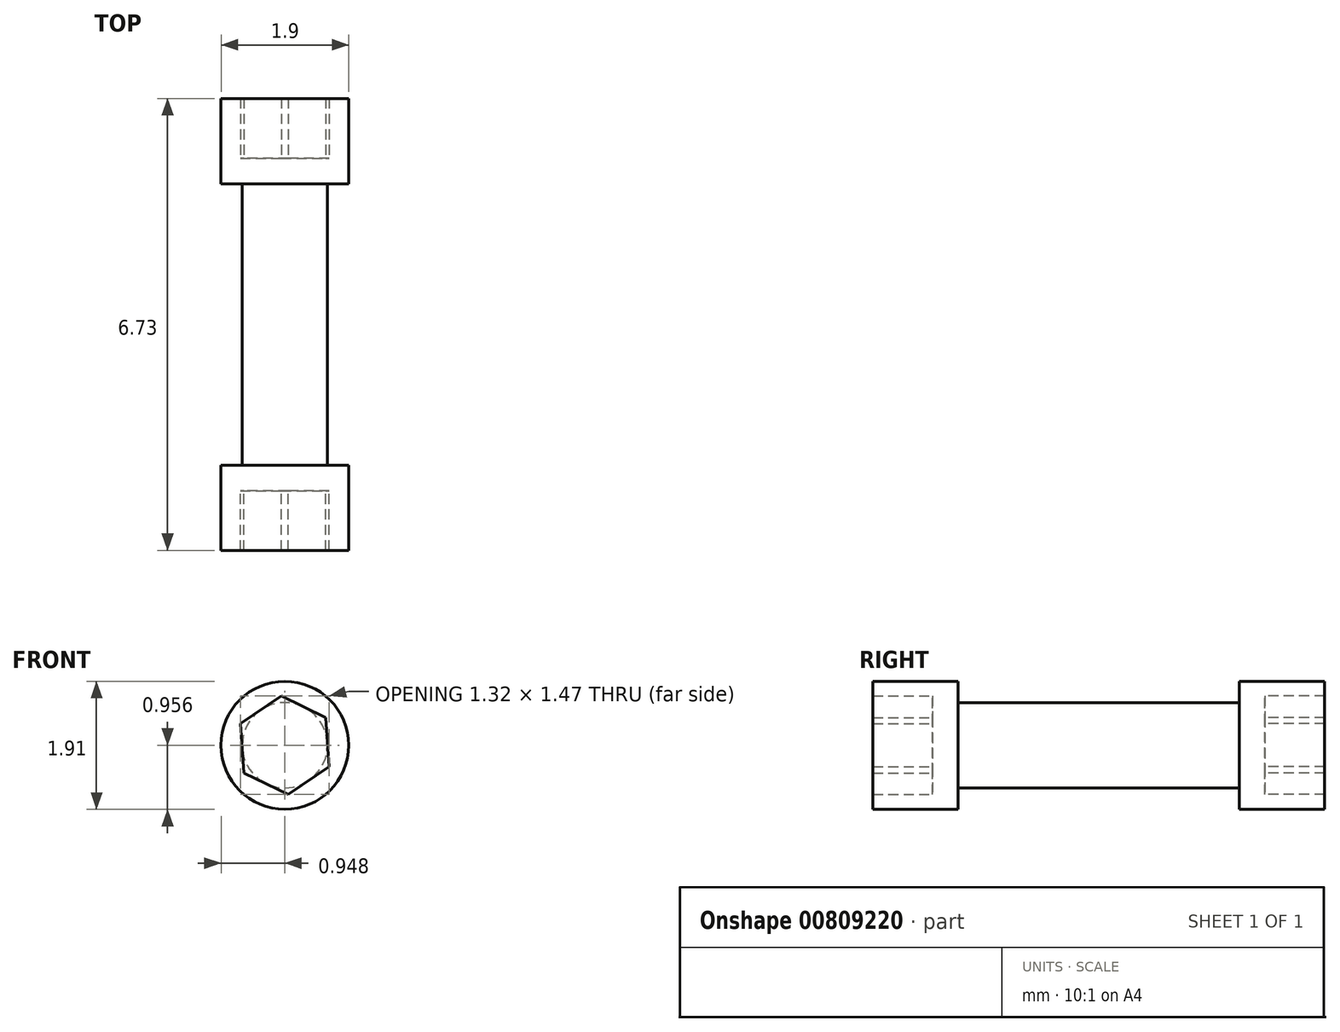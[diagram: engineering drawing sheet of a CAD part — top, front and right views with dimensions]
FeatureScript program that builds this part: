
annotation { "Feature Type Name" : "Feature", "Feature Type Description" : "" }
export const myFeature = defineFeature(function(context is Context, id is Id, definition is map)
    precondition{}
    {
        {
            var Q0;
            Q0=qCreatedBy(makeId("Front.planeOp"),FACE);
            var sketch = newSketch(context, id + "F0", { "sketchPlane" : qUnion([Q0])});
            skCircle(sketch, "E0", {"center": v(-50.83, 29.97) * mm, "radius": 0.64 * mm});
            skCircle(sketch, "E1", {"center": v(-50.83, 29.97) * mm, "radius": 0.95 * mm});
            skCircle(sketch, "E2.cCircle", {"center": v(-50.83, 29.97) * mm, "radius": 0.64 * mm, "construction": true});
            skLineSegment(sketch, "E2.0", {"start": v(-51.44, 29.56) * mm, "end": v(-51.49, 30.29) * mm});
            skLineSegment(sketch, "E2.1", {"start": v(-51.49, 30.29) * mm, "end": v(-50.88, 30.7) * mm});
            skLineSegment(sketch, "E2.2", {"start": v(-50.88, 30.7) * mm, "end": v(-50.22, 30.37) * mm});
            skLineSegment(sketch, "E2.3", {"start": v(-50.22, 30.37) * mm, "end": v(-50.17, 29.64) * mm});
            skLineSegment(sketch, "E2.4", {"start": v(-50.17, 29.64) * mm, "end": v(-50.78, 29.23) * mm});
            skLineSegment(sketch, "E2.5", {"start": v(-50.78, 29.23) * mm, "end": v(-51.44, 29.56) * mm});
            skPoint(sketch, "E2.0.midPoint", {"position": v(-51.47, 29.92) * mm});
            skSolve(sketch);
        }
        {
            var Q0;
            {var subQ0=sQuery(id+"F0.wireOp",EDGE,"E0");var subQ4=makeQuery(id+"F0.imprint","INTERSECT",VERTEX,{"derivedFrom":[subQ0,sQuery(id+"F0.wireOp",EDGE,"E2.2")]});Q0=makeQuery(id+"F0.imprint","IMPRINT",FACE,{"disambiguationData":[TD([[makeQuery(id+"F0.imprint","IMPRINT",EDGE,{"disambiguationData":[TD([[subQ4,1.0]])],"derivedFrom":subQ0}),1.0]])]});}
            extrude(context, id + "F1", {"entities" : qUnion([Q0]), "oppositeDirection" : true, "depth" : 2.1 * mm, "offsetDistance" : 25.4 * mm});
        }
        {
            var Q0;
            {var subQ0=sQuery(id+"F0.wireOp",EDGE,"E2.2");var subQ1=sQuery(id+"F0.wireOp",EDGE,"E0");var subQ2=makeQuery(id+"F0.imprint","INTERSECT",VERTEX,{"derivedFrom":[subQ1,subQ0]});Q0=makeQuery(id+"F0.imprint","IMPRINT",FACE,{"disambiguationData":[TD([[makeQuery(id+"F0.imprint","IMPRINT",EDGE,{"disambiguationData":[TD([[subQ2,1.0]])],"derivedFrom":subQ1}),-1.0]])]});}
            var Q1;
            {var subQ0=sQuery(id+"F0.wireOp",EDGE,"E2.2");var subQ1=sQuery(id+"F0.wireOp",EDGE,"E0");var subQ2=makeQuery(id+"F0.imprint","INTERSECT",VERTEX,{"derivedFrom":[subQ1,subQ0]});Q1=makeQuery(id+"F0.imprint","IMPRINT",FACE,{"disambiguationData":[TD([[makeQuery(id+"F0.imprint","IMPRINT",EDGE,{"disambiguationData":[TD([[subQ2,-1.0]])],"derivedFrom":subQ1}),-1.0]])]});}
            var Q2;
            {var subQ0=sQuery(id+"F0.wireOp",EDGE,"E2.5");var subQ1=sQuery(id+"F0.wireOp",EDGE,"E0");var subQ2=makeQuery(id+"F0.imprint","INTERSECT",VERTEX,{"derivedFrom":[subQ1,subQ0]});Q2=makeQuery(id+"F0.imprint","IMPRINT",FACE,{"disambiguationData":[TD([[makeQuery(id+"F0.imprint","IMPRINT",EDGE,{"disambiguationData":[TD([[subQ2,-1.0]])],"derivedFrom":subQ1}),-1.0]])]});}
            var Q3;
            {var subQ0=sQuery(id+"F0.wireOp",EDGE,"E2.0");var subQ1=sQuery(id+"F0.wireOp",EDGE,"E0");var subQ2=makeQuery(id+"F0.imprint","INTERSECT",VERTEX,{"derivedFrom":[subQ1,subQ0]});Q3=makeQuery(id+"F0.imprint","IMPRINT",FACE,{"disambiguationData":[TD([[makeQuery(id+"F0.imprint","IMPRINT",EDGE,{"disambiguationData":[TD([[subQ2,-1.0]])],"derivedFrom":subQ1}),-1.0]])]});}
            var Q4;
            {var subQ0=sQuery(id+"F0.wireOp",EDGE,"E2.3");var subQ1=sQuery(id+"F0.wireOp",EDGE,"E0");var subQ2=makeQuery(id+"F0.imprint","INTERSECT",VERTEX,{"derivedFrom":[subQ1,subQ0]});Q4=makeQuery(id+"F0.imprint","IMPRINT",FACE,{"disambiguationData":[TD([[makeQuery(id+"F0.imprint","IMPRINT",EDGE,{"disambiguationData":[TD([[subQ2,1.0]])],"derivedFrom":subQ1}),-1.0]])]});}
            var Q5;
            {var subQ0=sQuery(id+"F0.wireOp",EDGE,"E2.1");var subQ1=sQuery(id+"F0.wireOp",EDGE,"E0");var subQ2=makeQuery(id+"F0.imprint","INTERSECT",VERTEX,{"derivedFrom":[subQ1,subQ0]});Q5=makeQuery(id+"F0.imprint","IMPRINT",FACE,{"disambiguationData":[TD([[makeQuery(id+"F0.imprint","IMPRINT",EDGE,{"disambiguationData":[TD([[subQ2,-1.0]])],"derivedFrom":subQ1}),-1.0]])]});}
            var Q6;
            Q6=makeQuery(id+"F0.imprint","IMPRINT",FACE,{"disambiguationData":[TD([[makeQuery(id+"F0.imprint","IMPRINT",EDGE,{"derivedFrom":sQuery(id+"F0.wireOp",EDGE,"E1")}),1.0]])]});
            var Q7;
            {var subQ0=sQuery(id+"F0.wireOp",EDGE,"E0");var subQ4=makeQuery(id+"F0.imprint","INTERSECT",VERTEX,{"derivedFrom":[subQ0,sQuery(id+"F0.wireOp",EDGE,"E2.2")]});Q7=makeQuery(id+"F0.imprint","IMPRINT",FACE,{"disambiguationData":[TD([[makeQuery(id+"F0.imprint","IMPRINT",EDGE,{"disambiguationData":[TD([[subQ4,1.0]])],"derivedFrom":subQ0}),1.0]])]});}
            extrude(context, id + "F2", {"entities" : qUnion([Q0, Q1, Q2, Q3, Q4, Q5, Q6, Q7]), "operationType" : NewBodyOperationType.ADD, "depth" : 0.38 * mm, "offsetDistance" : 25.4 * mm});
        }
        {
            var Q0;
            Q0=makeQuery(id+"F2.opExtrude","CAP_FACE",FACE,{"disambiguationData":[OSD([sQuery(id+"F0.wireOp",EDGE,"E1")])],"isStart":false});
            var sketch = newSketch(context, id + "F3", { "sketchPlane" : qUnion([Q0])});
            skCircle(sketch, "E3", {"center": v(-50.83, 29.97) * mm, "radius": 0.64 * mm});
            skCircle(sketch, "E4.cCircle", {"center": v(-50.83, 29.97) * mm, "radius": 0.64 * mm, "construction": true});
            skLineSegment(sketch, "E4.0", {"start": v(-50.89, 30.7) * mm, "end": v(-50.22, 30.38) * mm});
            skLineSegment(sketch, "E4.1", {"start": v(-50.22, 30.38) * mm, "end": v(-50.17, 29.65) * mm});
            skLineSegment(sketch, "E4.2", {"start": v(-50.17, 29.65) * mm, "end": v(-50.78, 29.23) * mm});
            skLineSegment(sketch, "E4.3", {"start": v(-50.78, 29.23) * mm, "end": v(-51.44, 29.55) * mm});
            skLineSegment(sketch, "E4.4", {"start": v(-51.44, 29.55) * mm, "end": v(-51.5, 30.29) * mm});
            skLineSegment(sketch, "E4.5", {"start": v(-51.5, 30.29) * mm, "end": v(-50.89, 30.7) * mm});
            skPoint(sketch, "E4.0.midPoint", {"position": v(-50.55, 30.54) * mm});
            skSolve(sketch);
        }
        {
            var Q0;
            Q0=makeQuery(id+"F3.imprint","IMPRINT",FACE,{"disambiguationData":[TD([[makeQuery(id+"F3.imprint","IMPRINT",EDGE,{"derivedFrom":makeQuery(id+"F2.opExtrude","CAP_EDGE",EDGE,{"disambiguationData":[OSD([sQuery(id+"F0.wireOp",EDGE,"E1")])],"isStart":false})}),1.0]])]});
            extrude(context, id + "F4", {"entities" : qUnion([Q0]), "operationType" : NewBodyOperationType.ADD, "depth" : 0.89 * mm, "offsetDistance" : 25.4 * mm});
        }
        {
            var Q0;
            Q0=makeQuery(id+"F1.opExtrude","SWEPT_BODY",BODY,{"disambiguationData":[OSD([sQuery(id+"F0.wireOp",EDGE,"E0")])]});
            var Q1;
            Q1=makeQuery(id+"F1.opExtrude","CAP_FACE",FACE,{"disambiguationData":[OSD([sQuery(id+"F0.wireOp",EDGE,"E0")])],"isStart":false});
            mirror(context, id + "F5", {"operationType" : NewBodyOperationType.ADD, "entities" : qUnion([Q0]), "mirrorPlane" : qUnion([Q1])});
        }
    });
